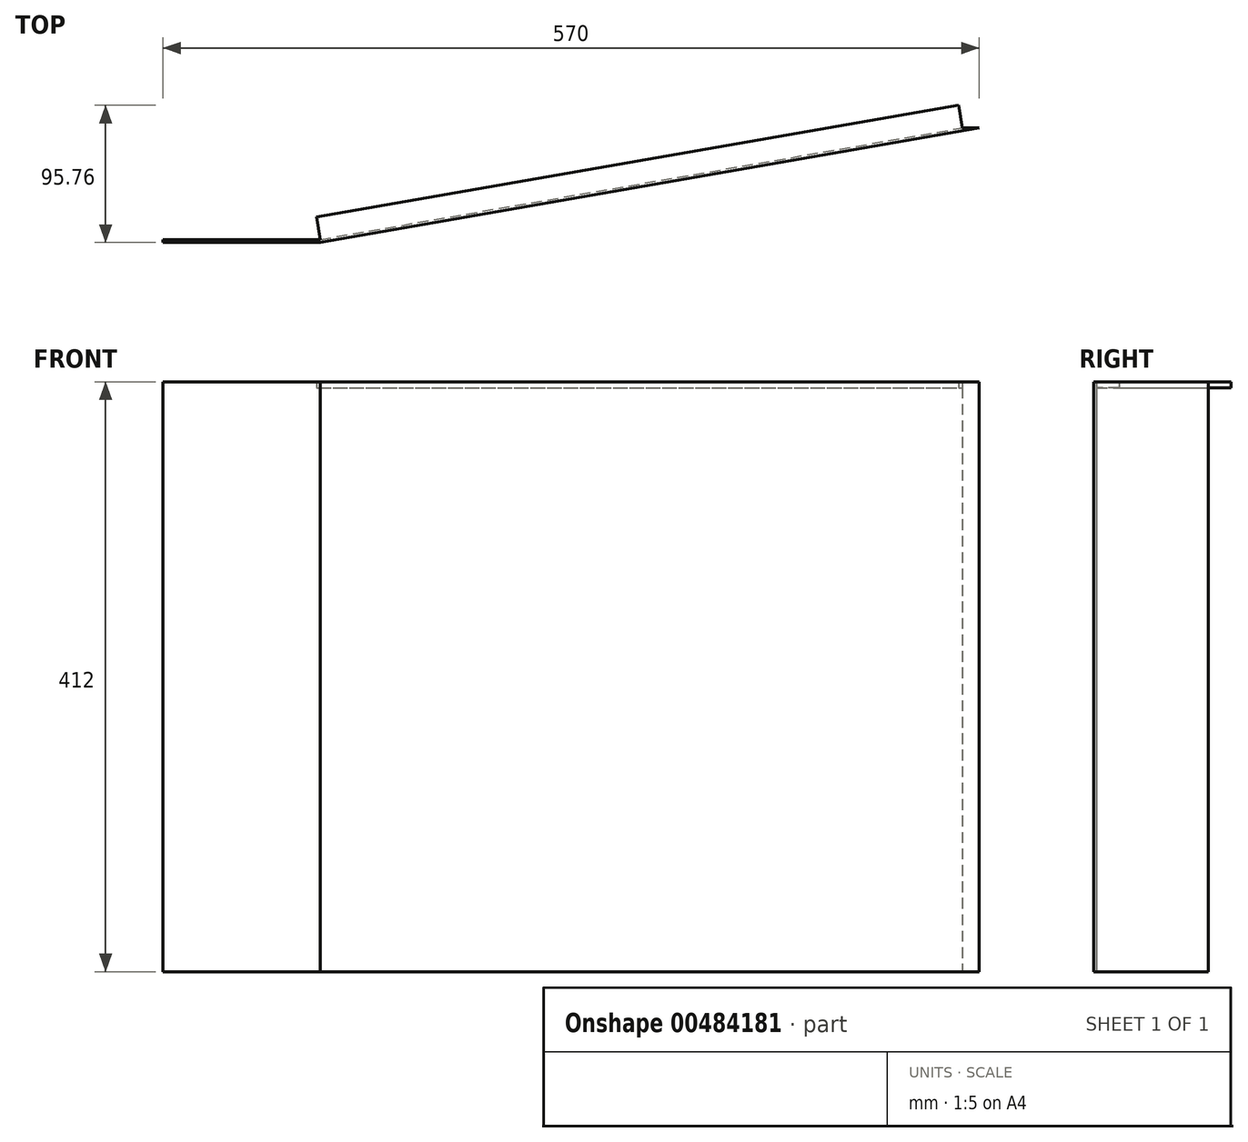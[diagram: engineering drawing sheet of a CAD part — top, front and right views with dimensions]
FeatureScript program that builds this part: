
annotation { "Feature Type Name" : "Feature", "Feature Type Description" : "" }
export const myFeature = defineFeature(function(context is Context, id is Id, definition is map)
    precondition{}
    {
        {
            var Q0;
            Q0=qCreatedBy(makeId("Top.planeOp"),FACE);
            var sketch = newSketch(context, id + "F0", { "sketchPlane" : qUnion([Q0])});
            skLineSegment(sketch, "E0", {"start": v(-104.37, 20.57) * mm, "end": v(5.63, 20.57) * mm});
            skLineSegment(sketch, "E1", {"start": v(5.63, 20.57) * mm, "end": v(5.63, 100.57) * mm});
            skLineSegment(sketch, "E2", {"start": v(5.63, 100.57) * mm, "end": v(465.63, 100.57) * mm});
            skLineSegment(sketch, "E3", {"start": v(5.63, 20.57) * mm, "end": v(465.63, 100.57) * mm});
            skLineSegment(sketch, "E4", {"start": v(465.63, 100.57) * mm, "end": v(465.28, 102.54) * mm});
            skLineSegment(sketch, "E5", {"start": v(5.63, 20.57) * mm, "end": v(5.63, 22.57) * mm});
            skLineSegment(sketch, "E6", {"start": v(5.63, 22.57) * mm, "end": v(465.28, 102.54) * mm});
            skLineSegment(sketch, "E7", {"start": v(-104.37, 20.57) * mm, "end": v(-104.37, 22.57) * mm});
            skLineSegment(sketch, "E8", {"start": v(-104.37, 22.57) * mm, "end": v(5.63, 22.57) * mm});
            skSolve(sketch);
        }
        {
            var Q0;
            Q0=makeQuery(id+"F0.imprint","IMPRINT",FACE,{"disambiguationData":[TD([[makeQuery(id+"F0.imprint","IMPRINT",EDGE,{"derivedFrom":sQuery(id+"F0.wireOp",EDGE,"E0")}),1.0]])]});
            var Q1;
            {var subQ0=sQuery(id+"F0.wireOp",EDGE,"E3");Q1=makeQuery(id+"F0.imprint","IMPRINT",FACE,{"disambiguationData":[TD([[makeQuery(id+"F0.imprint","IMPRINT",EDGE,{"derivedFrom":subQ0}),1.0]])]});}
            extrude(context, id + "F1", {"entities" : qUnion([Q0, Q1]), "depth" : 412 * mm, "offsetDistance" : 25 * mm});
        }
        {
            var Q0;
            Q0=makeQuery(id+"F1.opExtrude","SWEPT_FACE",FACE,{"disambiguationData":[OSD([sQuery(id+"F0.wireOp",EDGE,"E6")])]});
            var sketch = newSketch(context, id + "F2", { "sketchPlane" : qUnion([Q0])});
            skLineSegment(sketch, "E9.bottom", {"start": v(-9.41, 412) * mm, "end": v(-464.48, 412) * mm});
            skLineSegment(sketch, "E9.top", {"start": v(-9.41, 408) * mm, "end": v(-464.48, 408) * mm});
            skLineSegment(sketch, "E9.left", {"start": v(-9.41, 412) * mm, "end": v(-9.41, 408) * mm});
            skLineSegment(sketch, "E9.right", {"start": v(-464.48, 412) * mm, "end": v(-464.48, 408) * mm});
            skSolve(sketch);
        }
        {
            var Q0;
            Q0 = qSketchRegion(id + "F2", true);
            extrude(context, id + "F3", {"entities" : qUnion([Q0]), "operationType" : NewBodyOperationType.ADD, "depth" : 16 * mm, "offsetDistance" : 25 * mm});
        }
    });
